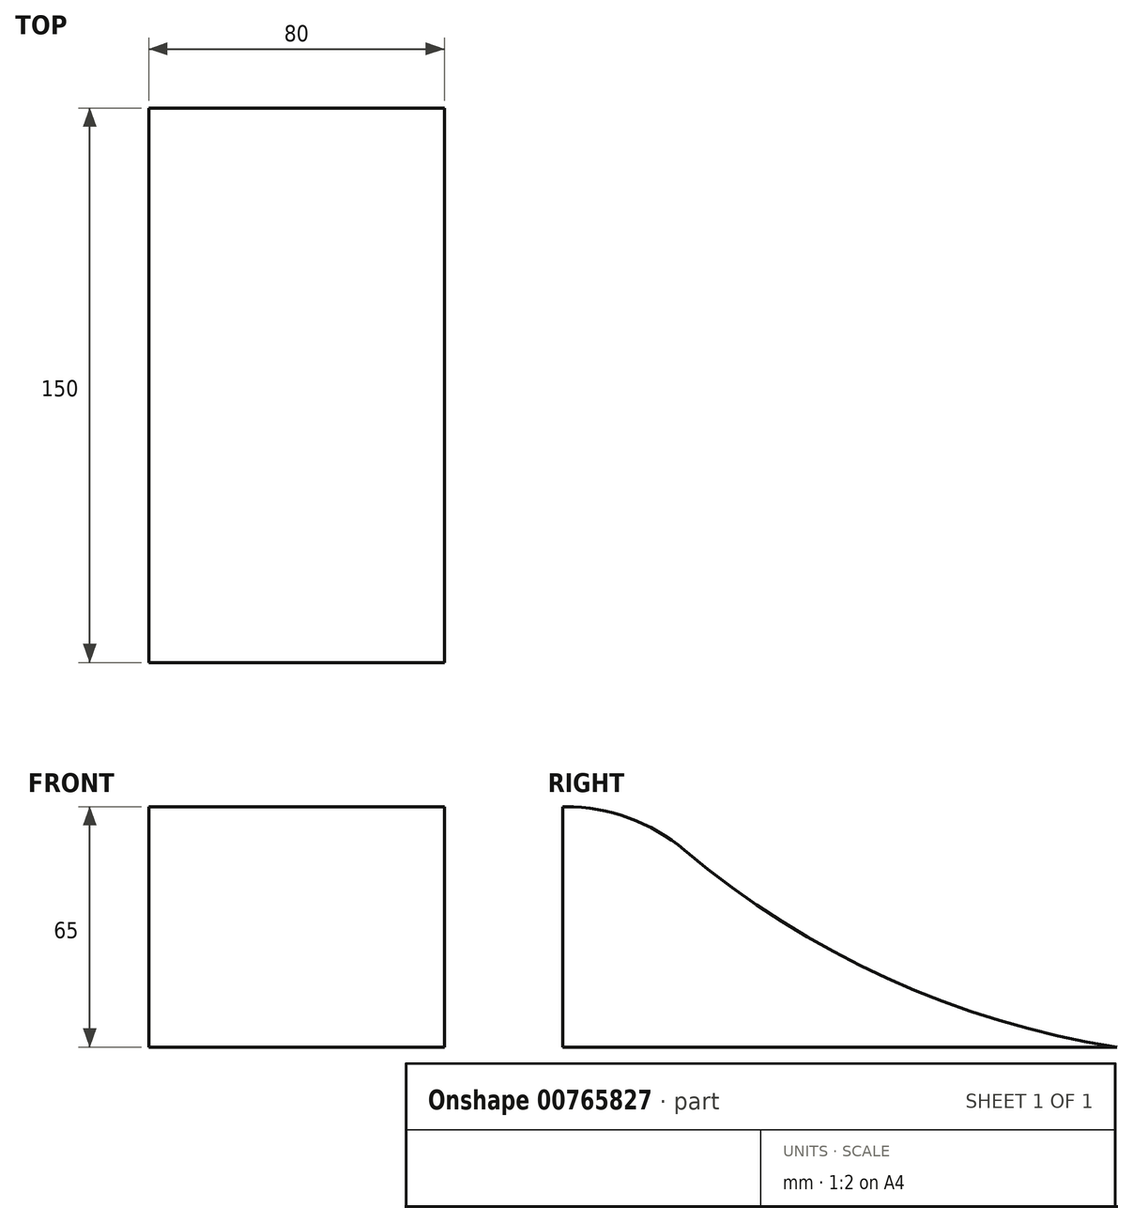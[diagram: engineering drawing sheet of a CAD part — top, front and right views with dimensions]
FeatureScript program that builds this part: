
annotation { "Feature Type Name" : "Feature", "Feature Type Description" : "" }
export const myFeature = defineFeature(function(context is Context, id is Id, definition is map)
    precondition{}
    {
        {
            var Q0;
            Q0=qCreatedBy(makeId("Right.planeOp"),FACE);
            var sketch = newSketch(context, id + "F0", { "sketchPlane" : qUnion([Q0])});
            skLineSegment(sketch, "E0", {"start": v(-74.8, 0) * mm, "end": v(75.2, 0) * mm});
            skLineSegment(sketch, "E1", {"start": v(-74.8, 0) * mm, "end": v(-74.8, 65) * mm});
            skLineSegment(sketch, "E2", {"start": v(-74.8, 65) * mm, "end": v(-54.8, 65) * mm});
            skArc(sketch, "E3", {"start": v(-54.8, 65) * mm, "mid": v(5.14, 22.36) * mm, "end": v(75.2, 0) * mm});
            skSolve(sketch);
        }
        {
            var Q0;
            Q0 = qSketchRegion(id + "F0", true);
            extrude(context, id + "F1", {"entities" : qUnion([Q0]), "depth" : 80 * mm, "offsetDistance" : 25 * mm});
        }
        {
            var Q0;
            Q0=makeQuery(id+"F1.opExtrude","SWEPT_EDGE",EDGE,{"disambiguationData":[OSD([sQuery(id+"F0.wireOp",EDGE,"E2"),sQuery(id+"F0.wireOp",EDGE,"E3")])]});
            fillet(context, id + "F2", {"entities" : qUnion([Q0]), "radius" : 50 * mm, "tangentPropagation" : true, "allowEdgeOverflow" : false});
        }
    });
